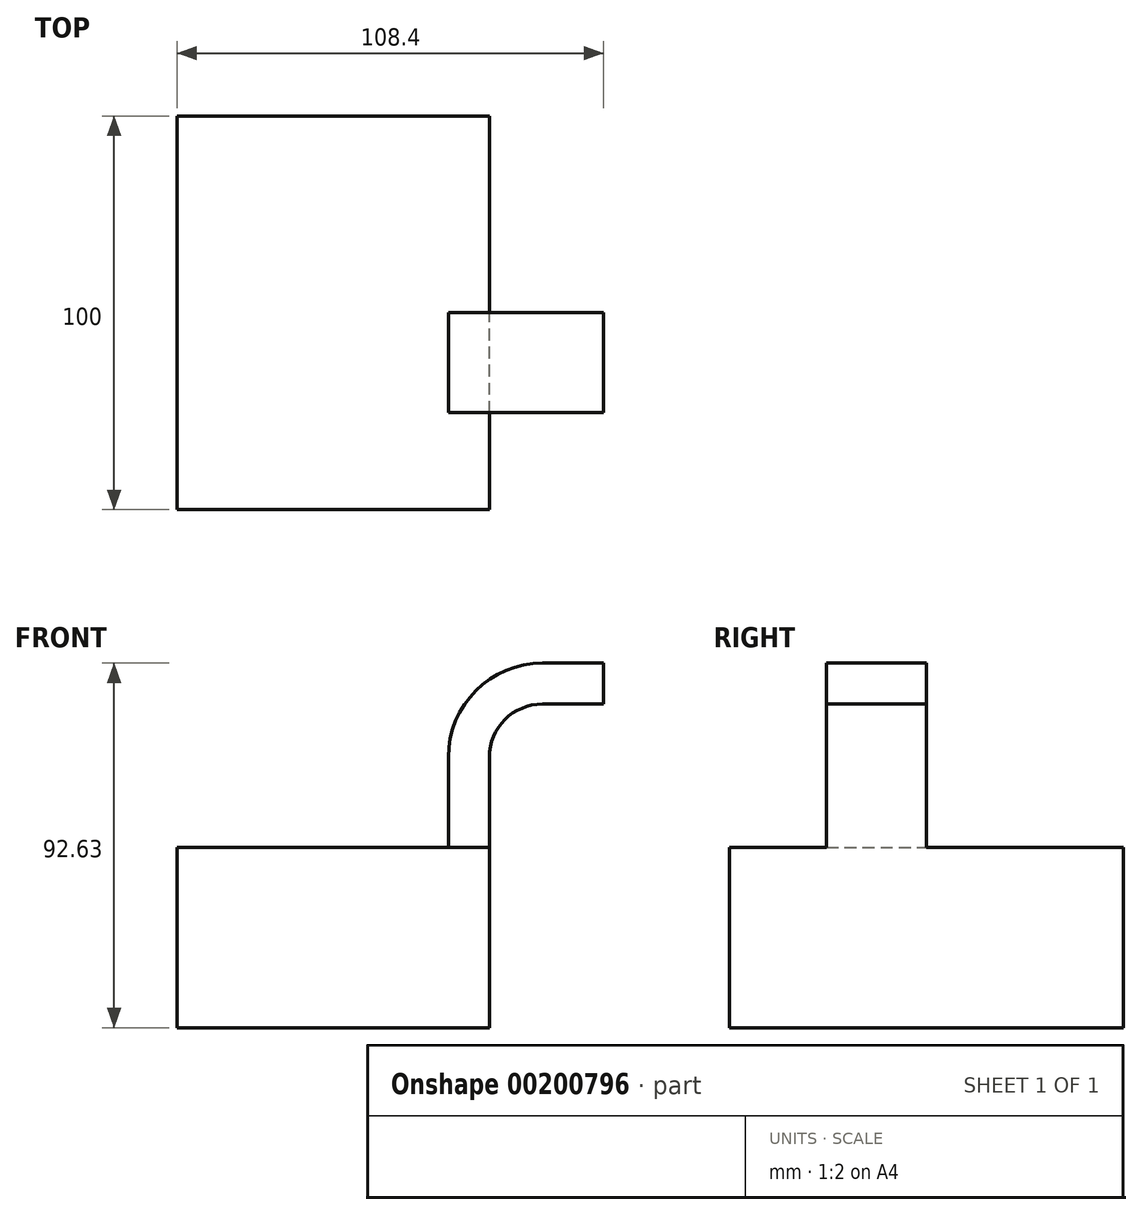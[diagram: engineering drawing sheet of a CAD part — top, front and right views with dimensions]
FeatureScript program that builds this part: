
annotation { "Feature Type Name" : "Feature", "Feature Type Description" : "" }
export const myFeature = defineFeature(function(context is Context, id is Id, definition is map)
    precondition{}
    {
        {
            var Q0;
            Q0=qCreatedBy(makeId("Front.planeOp"),FACE);
            var sketch = newSketch(context, id + "F0", { "sketchPlane" : qUnion([Q0])});
            skLineSegment(sketch, "E0.bottom", {"start": v(39.68, 22.9) * mm, "end": v(-39.68, 22.9) * mm});
            skLineSegment(sketch, "E0.top", {"start": v(39.68, -22.9) * mm, "end": v(-39.68, -22.9) * mm});
            skLineSegment(sketch, "E0.left", {"start": v(39.68, 22.9) * mm, "end": v(39.68, -22.9) * mm});
            skLineSegment(sketch, "E0.right", {"start": v(-39.68, 22.9) * mm, "end": v(-39.68, -22.9) * mm});
            skPoint(sketch, "E0.middle", {"position": v(0, 0) * mm});
            skLineSegment(sketch, "E1.bottom", {"start": v(68.72, 51.95) * mm, "end": v(103.08, 51.95) * mm});
            skLineSegment(sketch, "E1.top", {"start": v(68.72, 74.85) * mm, "end": v(103.08, 74.85) * mm});
            skLineSegment(sketch, "E1.left", {"start": v(68.72, 51.95) * mm, "end": v(68.72, 74.85) * mm});
            skLineSegment(sketch, "E1.right", {"start": v(103.08, 51.95) * mm, "end": v(103.08, 74.85) * mm});
            skLineSegment(sketch, "E2", {"start": v(39.68, 22.9) * mm, "end": v(39.68, 45.81) * mm});
            skArc(sketch, "E3", {"start": v(39.68, 45.81) * mm, "mid": v(43.63, 55.35) * mm, "end": v(53.17, 59.3) * mm});
            skLineSegment(sketch, "E4", {"start": v(53.17, 59.3) * mm, "end": v(85.12, 59.3) * mm});
            skLineSegment(sketch, "E5.0", {"start": v(53.17, 69.72) * mm, "end": v(85.12, 69.72) * mm});
            skArc(sketch, "E5.1", {"start": v(29.26, 45.81) * mm, "mid": v(36.26, 62.72) * mm, "end": v(53.17, 69.72) * mm});
            skLineSegment(sketch, "E5.2", {"start": v(29.26, 22.9) * mm, "end": v(29.26, 45.81) * mm});
            skLineSegment(sketch, "E6", {"start": v(85.12, 69.72) * mm, "end": v(85.12, 59.3) * mm});
            skFitSpline(sketch, "E7", {"points": [v(-39.68, 22.9) * mm, v(68.72, 74.85) * mm], "startDerivative": vector(2.27, 115.76) * mm, "endDerivative": vector(105.57, 1.62) * mm});
            skSolve(sketch);
        }
        {
            var Q0;
            Q0=makeQuery(id+"F0.imprint","IMPRINT",FACE,{"disambiguationData":[TD([[makeQuery(id+"F0.imprint","IMPRINT",EDGE,{"derivedFrom":sQuery(id+"F0.wireOp",EDGE,"E0.top")}),-1.0]])]});
            extrude(context, id + "F1", {"entities" : qUnion([Q0]), "endBound" : BoundingType.SYMMETRIC, "depth" : 100 * mm});
        }
        {
            var Q0;
            {var subQ1=sQuery(id+"F0.wireOp",EDGE,"E2");Q0=makeQuery(id+"F0.imprint","IMPRINT",FACE,{"disambiguationData":[TD([[makeQuery(id+"F0.imprint","IMPRINT",EDGE,{"derivedFrom":subQ1}),1.0]])]});}
            extrude(context, id + "F2", {"entities" : qUnion([Q0]), "operationType" : NewBodyOperationType.ADD, "depth" : 25.4 * mm});
        }
        {
            var Q0;
            {var subQ0=sQuery(id+"F0.wireOp",EDGE,"E5.1");Q0=makeQuery(id+"F0.imprint","IMPRINT",FACE,{"disambiguationData":[TD([[makeQuery(id+"F0.imprint","IMPRINT",EDGE,{"derivedFrom":subQ0}),1.0]])]});}
            extrude(context, id + "F3", {"entities" : qUnion([Q0]), "operationType" : NewBodyOperationType.ADD, "depth" : 12.7 * mm});
        }
    });
